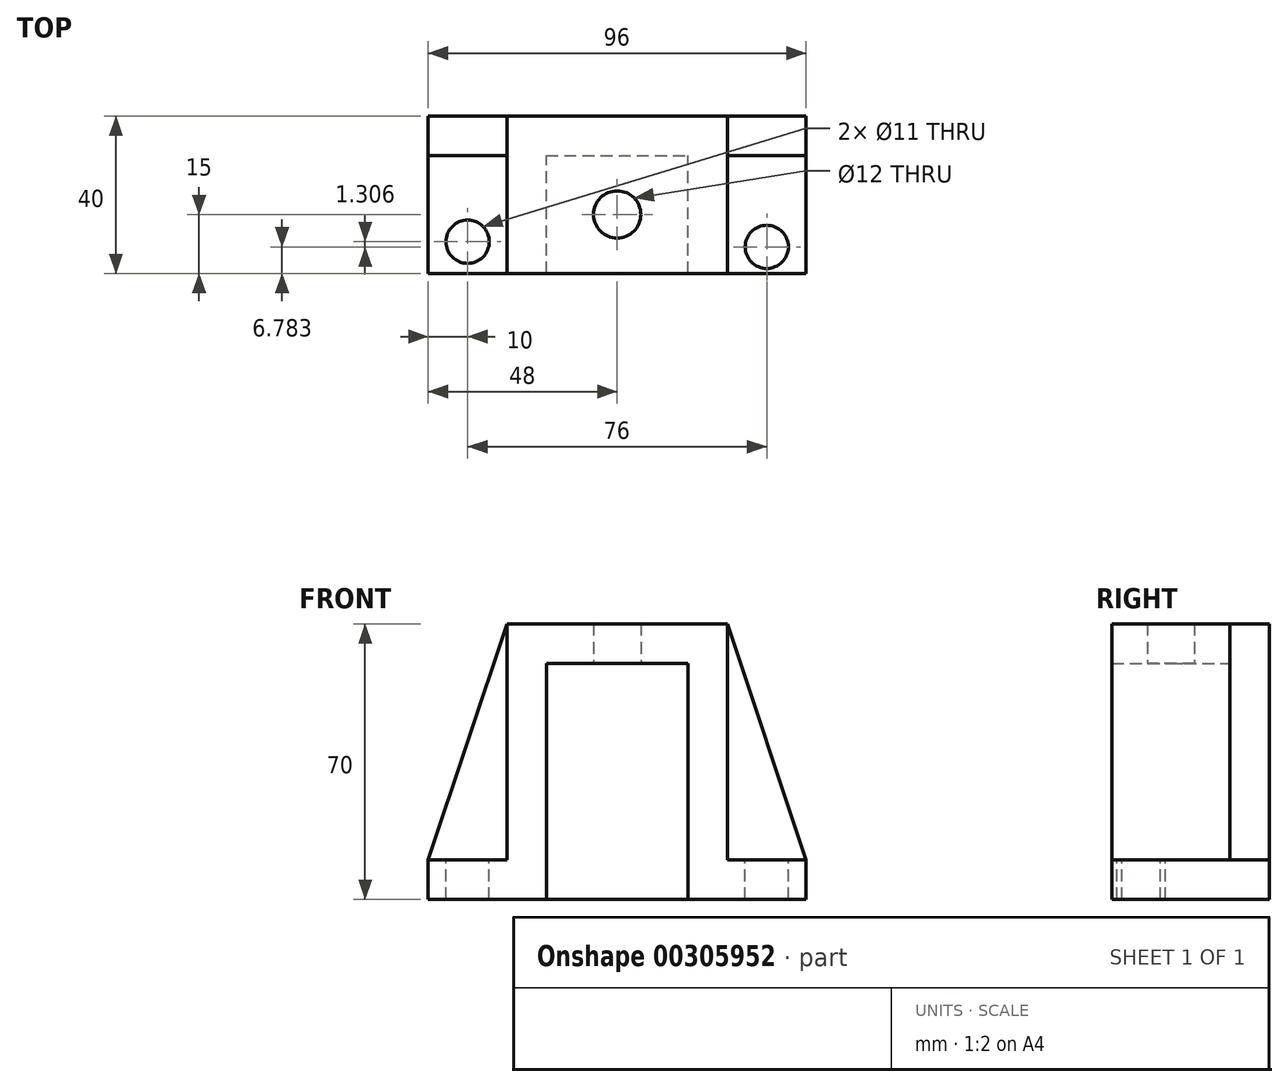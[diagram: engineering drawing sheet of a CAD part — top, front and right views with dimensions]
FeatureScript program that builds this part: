
annotation { "Feature Type Name" : "Feature", "Feature Type Description" : "" }
export const myFeature = defineFeature(function(context is Context, id is Id, definition is map)
    precondition{}
    {
        {
            var Q0;
            Q0=qCreatedBy(makeId("Front.planeOp"),FACE);
            var sketch = newSketch(context, id + "F0", { "sketchPlane" : qUnion([Q0])});
            skLineSegment(sketch, "E0", {"start": v(-48, 0) * mm, "end": v(-48, -10) * mm});
            skLineSegment(sketch, "E1", {"start": v(-48, -10) * mm, "end": v(-18, -10) * mm});
            skLineSegment(sketch, "E2", {"start": v(-18, -10) * mm, "end": v(-18, 50) * mm});
            skLineSegment(sketch, "E3", {"start": v(-18, 50) * mm, "end": v(18, 50) * mm});
            skLineSegment(sketch, "E4", {"start": v(18, 50) * mm, "end": v(18, -10) * mm});
            skLineSegment(sketch, "E5", {"start": v(18, -10) * mm, "end": v(48, -10) * mm});
            skLineSegment(sketch, "E6", {"start": v(48, -10) * mm, "end": v(48, 0) * mm});
            skLineSegment(sketch, "E7", {"start": v(48, 0) * mm, "end": v(28, 0) * mm});
            skLineSegment(sketch, "E8", {"start": v(28, 0) * mm, "end": v(28, 60) * mm});
            skLineSegment(sketch, "E9", {"start": v(28, 60) * mm, "end": v(-28, 60) * mm});
            skLineSegment(sketch, "E10", {"start": v(-28, 60) * mm, "end": v(-28, 0) * mm});
            skLineSegment(sketch, "E11", {"start": v(-28, 0) * mm, "end": v(-48, 0) * mm});
            skLineSegment(sketch, "E12", {"start": v(-28, 60) * mm, "end": v(-48, 0) * mm});
            skLineSegment(sketch, "E13", {"start": v(28, 60) * mm, "end": v(48, 0) * mm});
            skLineSegment(sketch, "E14", {"start": v(-18, -10) * mm, "end": v(18, -10) * mm});
            skSolve(sketch);
        }
        {
            var Q0;
            Q0=makeQuery(id+"F0.imprint","IMPRINT",FACE,{"disambiguationData":[TD([[makeQuery(id+"F0.imprint","IMPRINT",EDGE,{"derivedFrom":sQuery(id+"F0.wireOp",EDGE,"E0")}),1.0]])]});
            extrude(context, id + "F1", {"entities" : qUnion([Q0]), "depth" : 40 * mm});
        }
        {
            var Q0;
            Q0=makeQuery(id+"F0.imprint","IMPRINT",FACE,{"disambiguationData":[TD([[makeQuery(id+"F0.imprint","IMPRINT",EDGE,{"derivedFrom":sQuery(id+"F0.wireOp",EDGE,"E10")}),-1.0]])]});
            var Q1;
            Q1=makeQuery(id+"F0.imprint","IMPRINT",FACE,{"disambiguationData":[TD([[makeQuery(id+"F0.imprint","IMPRINT",EDGE,{"derivedFrom":sQuery(id+"F0.wireOp",EDGE,"E7")}),-1.0]])]});
            var Q2;
            Q2=makeQuery(id+"F0.imprint","IMPRINT",FACE,{"disambiguationData":[TD([[makeQuery(id+"F0.imprint","IMPRINT",EDGE,{"derivedFrom":sQuery(id+"F0.wireOp",EDGE,"E2")}),-1.0]])]});
            extrude(context, id + "F2", {"entities" : qUnion([Q0, Q1, Q2]), "operationType" : NewBodyOperationType.ADD, "depth" : 10 * mm});
        }
        {
            var Q0;
            Q0=qCreatedBy(makeId("Top.planeOp"),FACE);
            var sketch = newSketch(context, id + "F3", { "sketchPlane" : qUnion([Q0])});
            skCircle(sketch, "E15", {"center": v(-38, -31.91) * mm, "radius": 5.5 * mm});
            skCircle(sketch, "E16", {"center": v(38, -33.22) * mm, "radius": 5.5 * mm});
            skCircle(sketch, "E17", {"center": v(0, -25) * mm, "radius": 6 * mm});
            skSolve(sketch);
        }
        {
            var Q0;
            Q0=makeQuery(id+"F3.imprint","IMPRINT",FACE,{"disambiguationData":[TD([[makeQuery(id+"F3.imprint","IMPRINT",EDGE,{"derivedFrom":sQuery(id+"F3.wireOp",EDGE,"E15")}),1.0]])]});
            var Q1;
            Q1=makeQuery(id+"F3.imprint","IMPRINT",FACE,{"disambiguationData":[TD([[makeQuery(id+"F3.imprint","IMPRINT",EDGE,{"derivedFrom":sQuery(id+"F3.wireOp",EDGE,"E16")}),1.0]])]});
            extrude(context, id + "F4", {"entities" : qUnion([Q0, Q1]), "operationType" : NewBodyOperationType.REMOVE, "oppositeDirection" : true, "depth" : 10 * mm});
        }
        {
            var Q0;
            Q0=makeQuery(id+"F3.imprint","IMPRINT",FACE,{"disambiguationData":[TD([[makeQuery(id+"F3.imprint","IMPRINT",EDGE,{"derivedFrom":sQuery(id+"F3.wireOp",EDGE,"E17")}),1.0]])]});
            extrude(context, id + "F5", {"entities" : qUnion([Q0]), "operationType" : NewBodyOperationType.REMOVE, "depth" : 60 * mm});
        }
    });
